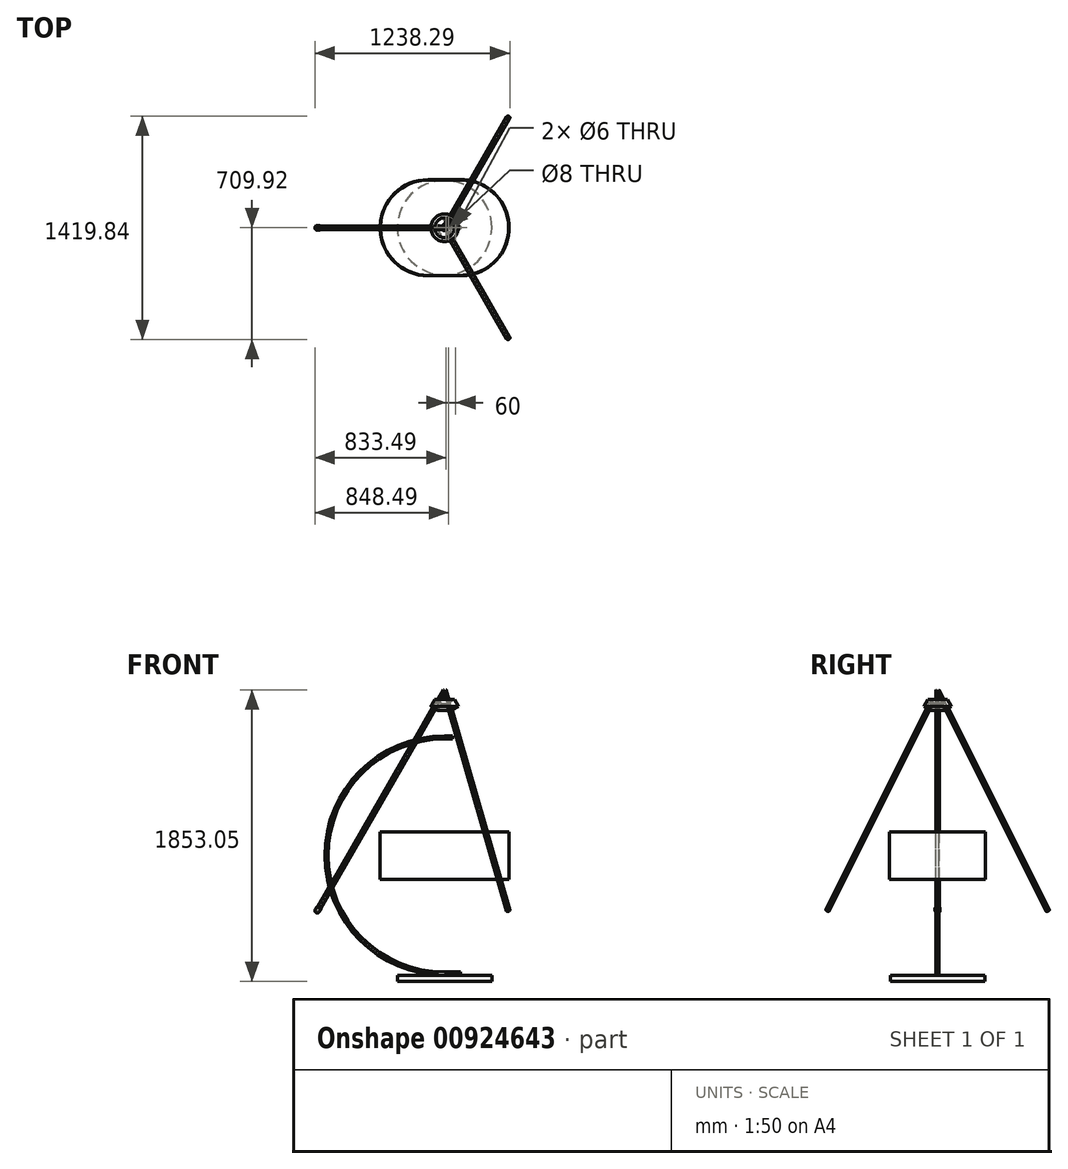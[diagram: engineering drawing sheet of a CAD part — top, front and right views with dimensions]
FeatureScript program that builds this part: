
annotation { "Feature Type Name" : "Feature", "Feature Type Description" : "" }
export const myFeature = defineFeature(function(context is Context, id is Id, definition is map)
    precondition{}
    {
        {
            var Q0;
            Q0=qCreatedBy(makeId("Top.planeOp"),FACE);
            var sketch = newSketch(context, id + "F0", { "sketchPlane" : qUnion([Q0])});
            skArc(sketch, "E0", {"start": v(-105, 305) * mm, "mid": v(-410, 0) * mm, "end": v(-105, -305) * mm});
            skArc(sketch, "E1", {"start": v(105, -305) * mm, "mid": v(410, 0) * mm, "end": v(105, 305) * mm});
            skLineSegment(sketch, "E2", {"start": v(-105, 305) * mm, "end": v(105, 305) * mm});
            skLineSegment(sketch, "E3", {"start": v(-105, -305) * mm, "end": v(105, -305) * mm});
            skSolve(sketch);
        }
        {
            var Q0;
            Q0=makeQuery(id+"F0.imprint","IMPRINT",FACE,{"disambiguationData":[TD([[makeQuery(id+"F0.imprint","IMPRINT",EDGE,{"derivedFrom":sQuery(id+"F0.wireOp",EDGE,"E0")}),1.0]])]});
            extrude(context, id + "F1", {"entities" : qUnion([Q0]), "depth" : 300 * mm, "offsetDistance" : 25 * mm});
        }
        {
            var Q0;
            Q0=makeQuery(id+"F1.opExtrude","CAP_FACE",FACE,{"disambiguationData":[OSD([sQuery(id+"F0.wireOp",EDGE,"E0"),sQuery(id+"F0.wireOp",EDGE,"E1"),sQuery(id+"F0.wireOp",EDGE,"E2"),sQuery(id+"F0.wireOp",EDGE,"E3")])],"isStart":false});
            shell(context, id + "F2", {"entities" : qUnion([Q0]), "thickness" : 2.5 * mm});
        }
        {
            var Q0;
            Q0=qCreatedBy(makeId("Front.planeOp"),FACE);
            var sketch = newSketch(context, id + "F3", { "sketchPlane" : qUnion([Q0])});
            skArc(sketch, "E4", {"start": v(0, -600) * mm, "mid": v(-750, 150) * mm, "end": v(0, 900) * mm});
            skSolve(sketch);
        }
        {
            var Q0;
            Q0=qCreatedBy(makeId("Right.planeOp"),FACE);
            var sketch = newSketch(context, id + "F4", { "sketchPlane" : qUnion([Q0])});
            skLineSegment(sketch, "E5.bottom", {"start": v(10, -590) * mm, "end": v(-10, -590) * mm});
            skLineSegment(sketch, "E5.top", {"start": v(10, -610) * mm, "end": v(-10, -610) * mm});
            skLineSegment(sketch, "E5.left", {"start": v(10, -590) * mm, "end": v(10, -610) * mm});
            skLineSegment(sketch, "E5.right", {"start": v(-10, -590) * mm, "end": v(-10, -610) * mm});
            skSolve(sketch);
        }
        {
            var Q0;
            Q0=makeQuery(id+"F4.imprint","IMPRINT",FACE,{"disambiguationData":[TD([[makeQuery(id+"F4.imprint","IMPRINT",EDGE,{"derivedFrom":sQuery(id+"F4.wireOp",EDGE,"E5.bottom")}),1.0]])]});
            var Q1;
            Q1=sQuery(id+"F3.wireOp",EDGE,"E4");
            sweep(context, id + "F5", {"profiles" : qUnion([Q0]), "path" : qUnion([Q1])});
        }
        {
            var Q0;
            Q0=makeQuery(id+"F5.opSweep","CAP_FACE",FACE,{"disambiguationData":[OSD([sQuery(id+"F3.wireOp",VERTEX,"E4.start"),sQuery(id+"F4.wireOp",EDGE,"E5.bottom"),sQuery(id+"F4.wireOp",EDGE,"E5.top"),sQuery(id+"F4.wireOp",EDGE,"E5.left"),sQuery(id+"F4.wireOp",EDGE,"E5.right")])],"isStart":true});
            extrude(context, id + "F6", {"entities" : qUnion([Q0]), "operationType" : NewBodyOperationType.ADD, "depth" : 100 * mm, "offsetDistance" : 25 * mm});
        }
        {
            var Q0;
            Q0=makeQuery(id+"F5.opSweep","CAP_FACE",FACE,{"disambiguationData":[OSD([sQuery(id+"F3.wireOp",VERTEX,"E4.end"),sQuery(id+"F4.wireOp",EDGE,"E5.bottom"),sQuery(id+"F4.wireOp",EDGE,"E5.top"),sQuery(id+"F4.wireOp",EDGE,"E5.left"),sQuery(id+"F4.wireOp",EDGE,"E5.right")])],"isStart":false});
            extrude(context, id + "F7", {"entities" : qUnion([Q0]), "operationType" : NewBodyOperationType.ADD, "depth" : 50 * mm, "offsetDistance" : 25 * mm});
        }
        {
            var Q0;
            Q0=qCreatedBy(makeId("Right.planeOp"),FACE);
            var sketch = newSketch(context, id + "F8", { "sketchPlane" : qUnion([Q0])});
            skLineSegment(sketch, "E6.bottom", {"start": v(0, -610) * mm, "end": v(300, -610) * mm});
            skLineSegment(sketch, "E6.top", {"start": v(0, -650) * mm, "end": v(300, -650) * mm});
            skLineSegment(sketch, "E6.left", {"start": v(0, -610) * mm, "end": v(0, -650) * mm});
            skLineSegment(sketch, "E6.right", {"start": v(300, -610) * mm, "end": v(300, -650) * mm});
            skSolve(sketch);
        }
        {
            var Q0;
            Q0=makeQuery(id+"F8.imprint","IMPRINT",FACE,{"disambiguationData":[TD([[makeQuery(id+"F8.imprint","IMPRINT",EDGE,{"derivedFrom":sQuery(id+"F8.wireOp",EDGE,"E6.bottom")}),-1.0]])]});
            var Q1;
            Q1=sQuery(id+"F8.wireOp",EDGE,"E6.left");
            revolve(context, id + "F9", {"surfaceOperationType" : NewSurfaceOperationType.NEW, "entities" : qUnion([Q0]), "axis" : qUnion([Q1]), "revolveType" : RevolveType.FULL});
        }
        {
            var Q0;
            Q0=qCreatedBy(makeId("Front.planeOp"),FACE);
            var sketch = newSketch(context, id + "F10", { "sketchPlane" : qUnion([Q0])});
            skLineSegment(sketch, "E7", {"start": v(-808.3, -200) * mm, "end": v(0, 1200) * mm});
            skLineSegment(sketch, "E8", {"start": v(0, 0) * mm, "end": v(0, 1200) * mm, "construction": true});
            skSolve(sketch);
        }
        {
            var Q0;
            Q0=qCreatedBy(makeId("Right.planeOp"),FACE);
            var sketch = newSketch(context, id + "F11", { "sketchPlane" : qUnion([Q0])});
            skLineSegment(sketch, "E9", {"start": v(0, 1200) * mm, "end": v(129.47, 1200) * mm, "construction": true});
            skSolve(sketch);
        }
        {
            var Q0;
            Q0=sQuery(id+"F11.wireOp",EDGE,"E9");
            var Q1;
            Q1=qCreatedBy(makeId("Top.planeOp"),FACE);
            cPlane(context, id + "F12", {"entities" : qUnion([Q0, Q1]), "cplaneType" : CPlaneType.LINE_ANGLE, "offset" : 25 * mm, "angle" : 30 * degree, "width" : 150 * mm, "height" : 150 * mm});
        }
        {
            var Q0;
            Q0=qCreatedBy(id+"F12.planeOp",FACE);
            var sketch = newSketch(context, id + "F13", { "sketchPlane" : qUnion([Q0])});
            skCircle(sketch, "E10", {"center": v(-600, 0) * mm, "radius": 11 * mm});
            skSolve(sketch);
        }
        {
            var Q0;
            Q0=makeQuery(id+"F13.imprint","IMPRINT",FACE,{"disambiguationData":[TD([[makeQuery(id+"F13.imprint","IMPRINT",EDGE,{"derivedFrom":sQuery(id+"F13.wireOp",EDGE,"E10")}),1.0]])]});
            var Q1;
            Q1=sQuery(id+"F10.wireOp",VERTEX,"E7.start");
            extrude(context, id + "F14", {"entities" : qUnion([Q0]), "endBound" : BoundingType.UP_TO_VERTEX, "depth" : 25 * mm, "endBoundEntityVertex" : qUnion([Q1]), "offsetDistance" : 25 * mm});
        }
        {
            var Q0;
            Q0=makeQuery(id+"F14.opExtrude","SWEPT_BODY",BODY,{"disambiguationData":[OSD([sQuery(id+"F13.wireOp",EDGE,"E10")])]});
            var Q1;
            Q1=sQuery(id+"F10.wireOp",EDGE,"E8");
            circularPattern(context, id + "F15", {"entities" : qUnion([Q0]), "axis" : qUnion([Q1]), "angle" : 360 * degree, "instanceCount" : 3, "equalSpace" : true});
        }
        {
            var Q0;
            Q0=qCreatedBy(makeId("Top.planeOp"),FACE);
            cPlane(context, id + "F16", {"entities" : qUnion([Q0]), "cplaneType" : CPlaneType.OFFSET, "offset" : 1100 * mm, "width" : 150 * mm, "height" : 150 * mm});
        }
        {
            var Q0;
            Q0=makeQuery(id+"F6.opExtrude","SWEPT_FACE",FACE,{"disambiguationData":[OSD([sQuery(id+"F3.wireOp",VERTEX,"E4.start"),sQuery(id+"F4.wireOp",EDGE,"E5.bottom")])]});
            var sketch = newSketch(context, id + "F17", { "sketchPlane" : qUnion([Q0])});
            skPoint(sketch, "E11", {"position": v(70, 0) * mm});
            skPoint(sketch, "E12", {"position": v(10, 0) * mm});
            skSolve(sketch);
        }
        {
            var Q0;
            Q0=sQuery(id+"F17.wireOp",VERTEX,"E11");
            var Q1;
            Q1=sQuery(id+"F17.wireOp",VERTEX,"E12");
            var Q2;
            Q2=makeQuery(id+"F5.opSweep","SWEPT_BODY",BODY,{"disambiguationData":[OSD([sQuery(id+"F3.wireOp",EDGE,"E4"),sQuery(id+"F4.wireOp",EDGE,"E5.bottom"),sQuery(id+"F4.wireOp",EDGE,"E5.top"),sQuery(id+"F4.wireOp",EDGE,"E5.left"),sQuery(id+"F4.wireOp",EDGE,"E5.right")])]});
            hole(context, id + "F18", {"style" : HoleStyle.C_SINK, "endStyle" : HoleEndStyle.THROUGH, "holeDiameter" : 6 * mm, "cSinkDiameter" : 10 * mm, "cSinkAngle" : 90 * degree, "majorDiameter" : 5 * mm, "isTappedThrough" : true, "tappedDepth" : 12 * mm, "tapClearance" : 3, "locations" : qUnion([Q0, Q1]), "scope" : qUnion([Q2])});
        }
        {
            var Q0;
            Q0=makeQuery(id+"F7.opExtrude","SWEPT_FACE",FACE,{"disambiguationData":[OSD([sQuery(id+"F3.wireOp",VERTEX,"E4.end"),sQuery(id+"F4.wireOp",EDGE,"E5.top")])]});
            var sketch = newSketch(context, id + "F19", { "sketchPlane" : qUnion([Q0])});
            skPoint(sketch, "E13", {"position": v(25, 0) * mm});
            skSolve(sketch);
        }
        {
            var Q0;
            Q0=sQuery(id+"F19.wireOp",VERTEX,"E13");
            var Q1;
            Q1=makeQuery(id+"F5.opSweep","SWEPT_BODY",BODY,{"disambiguationData":[OSD([sQuery(id+"F3.wireOp",EDGE,"E4"),sQuery(id+"F4.wireOp",EDGE,"E5.bottom"),sQuery(id+"F4.wireOp",EDGE,"E5.top"),sQuery(id+"F4.wireOp",EDGE,"E5.left"),sQuery(id+"F4.wireOp",EDGE,"E5.right")])]});
            hole(context, id + "F20", {"style" : HoleStyle.C_SINK, "endStyle" : HoleEndStyle.BLIND, "holeDiameter" : 8 * mm, "cSinkDiameter" : 10 * mm, "cSinkAngle" : 90 * degree, "majorDiameter" : 5 * mm, "holeDepth" : 20 * mm, "isTappedThrough" : true, "tappedDepth" : 12 * mm, "tapClearance" : 3, "locations" : qUnion([Q0]), "scope" : qUnion([Q1])});
        }
        {
            var Q0;
            Q0=qCreatedBy(makeId("Front.planeOp"),FACE);
            var sketch = newSketch(context, id + "F21", { "sketchPlane" : qUnion([Q0])});
            skLineSegment(sketch, "E14.0", {"start": v(-798.76, -205.5) * mm, "end": v(-817.82, -194.5) * mm, "construction": true});
            skPoint(sketch, "E15", {"position": v(-808.3, -200) * mm});
            skLineSegment(sketch, "E16", {"start": v(-808.3, -200) * mm, "end": v(-798.6, -205.6) * mm});
            skLineSegment(sketch, "E17", {"start": v(-798.6, -205.6) * mm, "end": v(-788.6, -188.28) * mm});
            skLineSegment(sketch, "E18", {"start": v(-788.6, -188.28) * mm, "end": v(-785.13, -190.28) * mm});
            skLineSegment(sketch, "E19", {"start": v(-785.13, -190.28) * mm, "end": v(-795.13, -207.6) * mm});
            skArc(sketch, "E20", {"start": v(-815.9, -213.16) * mm, "mid": v(-804.36, -214.68) * mm, "end": v(-795.13, -207.6) * mm});
            skLineSegment(sketch, "E21", {"start": v(-808.3, -200) * mm, "end": v(-815.9, -213.16) * mm});
            skSolve(sketch);
        }
        {
            var Q0;
            Q0=makeQuery(id+"F21.imprint","IMPRINT",FACE,{"disambiguationData":[TD([[makeQuery(id+"F21.imprint","IMPRINT",EDGE,{"derivedFrom":sQuery(id+"F21.wireOp",EDGE,"E16")}),-1.0]])]});
            var Q1;
            Q1=sQuery(id+"F21.wireOp",EDGE,"E21");
            revolve(context, id + "F22", {"surfaceOperationType" : NewSurfaceOperationType.NEW, "entities" : qUnion([Q0]), "axis" : qUnion([Q1]), "revolveType" : RevolveType.FULL});
        }
        {
            var Q0;
            Q0=makeQuery(id+"F15.opPattern","COPY",FACE,{"derivedFrom":makeQuery(id+"F14.opExtrude","CAP_FACE",FACE,{"disambiguationData":[OSD([sQuery(id+"F13.wireOp",EDGE,"E10")])],"isStart":true}),"instanceName":"1"});
            extrude(context, id + "F23", {"entities" : qUnion([Q0]), "operationType" : NewBodyOperationType.REMOVE, "oppositeDirection" : true, "depth" : 95 * mm, "offsetDistance" : 25 * mm});
        }
        {
            var Q0;
            Q0=makeQuery(id+"F14.opExtrude","CAP_FACE",FACE,{"disambiguationData":[OSD([sQuery(id+"F13.wireOp",EDGE,"E10")])],"isStart":true});
            extrude(context, id + "F24", {"entities" : qUnion([Q0]), "operationType" : NewBodyOperationType.REMOVE, "oppositeDirection" : true, "depth" : 95 * mm, "offsetDistance" : 25 * mm});
        }
        {
            var Q0;
            Q0=makeQuery(id+"F15.opPattern","COPY",FACE,{"derivedFrom":makeQuery(id+"F14.opExtrude","CAP_FACE",FACE,{"disambiguationData":[OSD([sQuery(id+"F13.wireOp",EDGE,"E10")])],"isStart":true}),"instanceName":"2"});
            extrude(context, id + "F25", {"entities" : qUnion([Q0]), "operationType" : NewBodyOperationType.REMOVE, "oppositeDirection" : true, "depth" : 95 * mm, "offsetDistance" : 25 * mm});
        }
        {
            var Q0;
            Q0=makeQuery(id+"F25.boolean.opBoolean","COPY",FACE,{"derivedFrom":makeQuery(id+"F25.opExtrude","CAP_FACE",FACE,{"disambiguationData":[OSD([sQuery(id+"F13.wireOp",EDGE,"E10")])],"isStart":false})});
            var sketch = newSketch(context, id + "F26", { "sketchPlane" : qUnion([Q0])});
            skCircle(sketch, "E22", {"center": v(268.33, 536.66) * mm, "radius": 11.3 * mm});
            skSolve(sketch);
        }
        {
            var Q0;
            Q0 = qSketchRegion(id + "F26", true);
            extrude(context, id + "F27", {"entities" : qUnion([Q0]), "oppositeDirection" : true, "depth" : 80 * mm, "offsetDistance" : 25 * mm});
        }
        {
            var Q0;
            Q0=makeQuery(id+"F27.opExtrude","SWEPT_BODY",BODY,{"disambiguationData":[OSD([sQuery(id+"F26.wireOp",EDGE,"E22")])]});
            var Q1;
            Q1=sQuery(id+"F10.wireOp",EDGE,"E8");
            circularPattern(context, id + "F28", {"entities" : qUnion([Q0]), "axis" : qUnion([Q1]), "angle" : 360 * degree, "instanceCount" : 3, "equalSpace" : true});
        }
        {
            var Q0;
            Q0=qCreatedBy(makeId("Front.planeOp"),FACE);
            var sketch = newSketch(context, id + "F29", { "sketchPlane" : qUnion([Q0])});
            skLineSegment(sketch, "E23", {"start": v(9.53, 1194.5) * mm, "end": v(-798.76, -205.5) * mm, "construction": true});
            skLineSegment(sketch, "E24", {"start": v(-44.22, 1073.41) * mm, "end": v(-19.22, 1116.71) * mm});
            skLineSegment(sketch, "E25", {"start": v(-19.22, 1116.71) * mm, "end": v(-62.52, 1141.71) * mm});
            skLineSegment(sketch, "E26", {"start": v(-62.52, 1141.71) * mm, "end": v(-87.52, 1098.41) * mm});
            skLineSegment(sketch, "E27", {"start": v(-87.52, 1098.41) * mm, "end": v(-44.22, 1073.41) * mm});
            skSolve(sketch);
        }
        {
            var Q0;
            Q0=makeQuery(id+"F29.imprint","IMPRINT",FACE,{"disambiguationData":[TD([[makeQuery(id+"F29.imprint","IMPRINT",EDGE,{"derivedFrom":sQuery(id+"F29.wireOp",EDGE,"E24")}),1.0]])]});
            var Q1;
            Q1=sQuery(id+"F10.wireOp",EDGE,"E8");
            revolve(context, id + "F30", {"surfaceOperationType" : NewSurfaceOperationType.NEW, "entities" : qUnion([Q0]), "axis" : qUnion([Q1]), "revolveType" : RevolveType.FULL});
        }
        {
            var Q0;
            Q0=makeQuery(id+"F27.opExtrude","SWEPT_BODY",BODY,{"disambiguationData":[OSD([sQuery(id+"F26.wireOp",EDGE,"E22")])]});
            var Q1;
            Q1=makeQuery(id+"F28.opPattern","COPY",BODY,{"derivedFrom":makeQuery(id+"F27.opExtrude","SWEPT_BODY",BODY,{"disambiguationData":[OSD([sQuery(id+"F26.wireOp",EDGE,"E22")])]}),"instanceName":"2"});
            var Q2;
            Q2=makeQuery(id+"F28.opPattern","COPY",BODY,{"derivedFrom":makeQuery(id+"F27.opExtrude","SWEPT_BODY",BODY,{"disambiguationData":[OSD([sQuery(id+"F26.wireOp",EDGE,"E22")])]}),"instanceName":"1"});
            var Q3;
            Q3=makeQuery(id+"F30.opRevolve","SWEPT_BODY",BODY,{"disambiguationData":[OSD([sQuery(id+"F29.wireOp",EDGE,"E24"),sQuery(id+"F29.wireOp",EDGE,"E25"),sQuery(id+"F29.wireOp",EDGE,"E26"),sQuery(id+"F29.wireOp",EDGE,"E27")])]});
            booleanBodies(context, id + "F31", {"operationType" : BooleanOperationType.SUBTRACTION, "tools" : qUnion([Q0, Q1, Q2]), "targets" : qUnion([Q3])});
        }
    });
